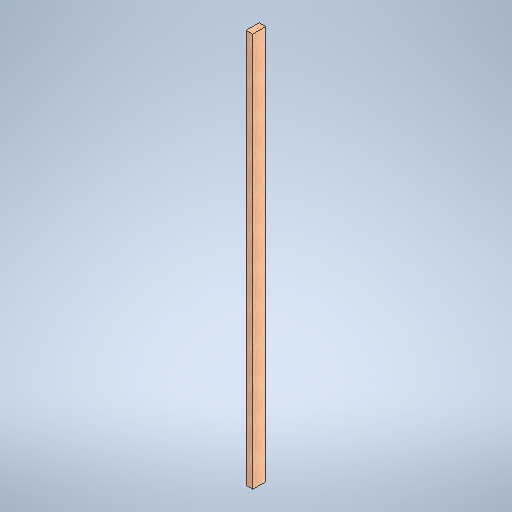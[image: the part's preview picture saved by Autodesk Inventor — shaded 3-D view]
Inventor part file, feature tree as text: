
AUTODESK INVENTOR PART (.ipt)
format: ipt  version: 2025 (Build 290162000, 162)  size: 292,352 bytes
history: native  units: in
note: dims shown in document units (in); Inventor stores cm internally (conversion verified against a paired STEP export)
features: extrude x1, sketch x1
ambient origin geometry x8: Origin, YZ Plane, XZ Plane, XY Plane, X Axis, Y Axis, Z Axis, Center Point
bodies: Solid1 (feature_tree)
feature tree (2):
  extrude  "Extrusion1"  Depth=4.0in
  sketch  "Sketch1"  dims[d0=2.0in d1=4.0in d2=120.0in d3=0.0in]
